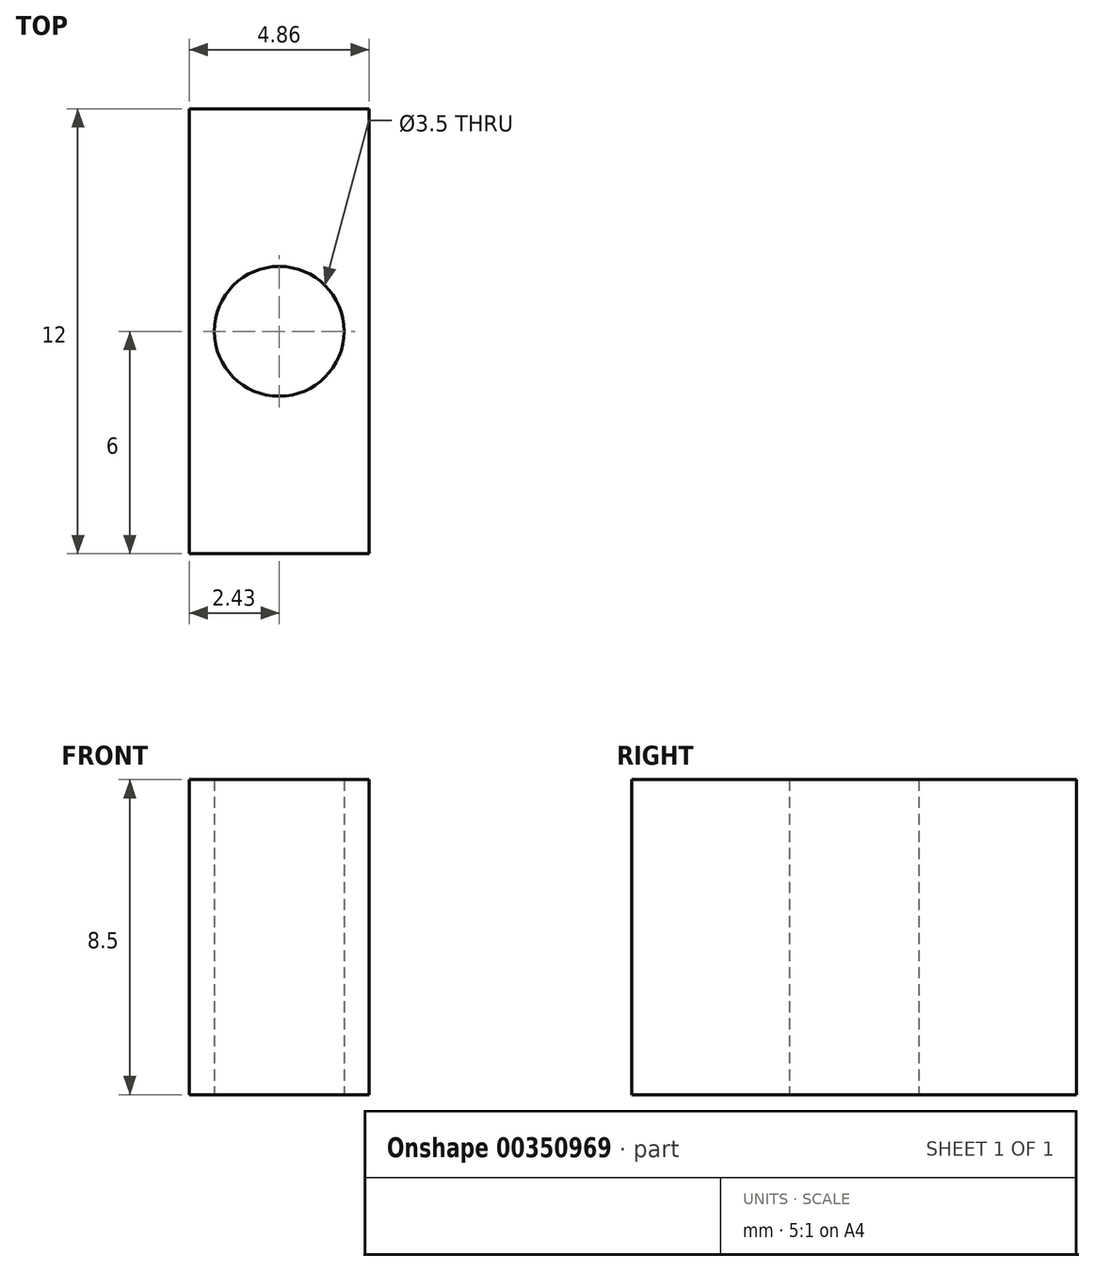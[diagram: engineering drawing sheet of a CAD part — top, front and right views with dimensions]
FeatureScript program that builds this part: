
annotation { "Feature Type Name" : "Feature", "Feature Type Description" : "" }
export const myFeature = defineFeature(function(context is Context, id is Id, definition is map)
    precondition{}
    {
        {
            var Q0;
            Q0=qCreatedBy(makeId("Top.planeOp"),FACE);
            var sketch = newSketch(context, id + "F0", { "sketchPlane" : qUnion([Q0])});
            skCircle(sketch, "E0", {"center": v(0, 0) * mm, "radius": 1.75 * mm});
            skLineSegment(sketch, "E1.bottom", {"start": v(-2.42, -6) * mm, "end": v(2.43, -6) * mm});
            skLineSegment(sketch, "E1.top", {"start": v(-2.43, 6) * mm, "end": v(2.42, 6) * mm});
            skLineSegment(sketch, "E1.left", {"start": v(-2.43, -6) * mm, "end": v(-2.43, 6) * mm});
            skLineSegment(sketch, "E1.right", {"start": v(2.43, -6) * mm, "end": v(2.42, 6) * mm});
            skSolve(sketch);
        }
        {
            var Q0;
            Q0=makeQuery(id+"F0.imprint","IMPRINT",FACE,{"disambiguationData":[TD([[makeQuery(id+"F0.imprint","IMPRINT",EDGE,{"derivedFrom":sQuery(id+"F0.wireOp",EDGE,"E0")}),-1.0]])]});
            extrude(context, id + "F1", {"entities" : qUnion([Q0]), "depth" : 8.5 * mm});
        }
    });
